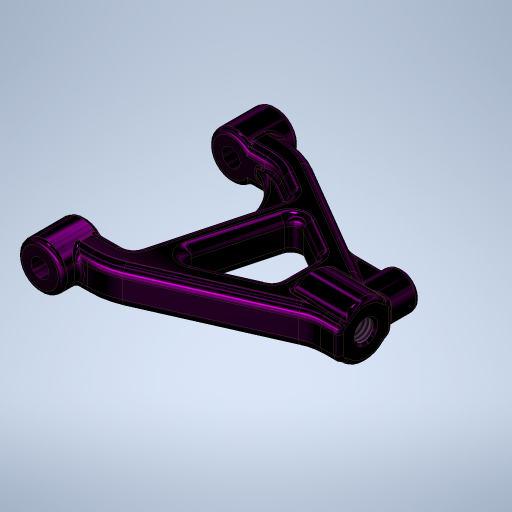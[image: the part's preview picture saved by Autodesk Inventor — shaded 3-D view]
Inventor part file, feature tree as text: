
AUTODESK INVENTOR PART (.ipt)
format: ipt  version: 2023.1 (Build 271208000, 208)  size: 1,221,120 bytes
history: native  units: in
note: dims shown in document units (in); Inventor stores cm internally (conversion verified against a paired STEP export)
features: fillet x19, sketch x11, extrude x6, rib x3, plane x2, hole x2, projected_geometry x2, chamfer x1
ambient origin geometry x8: Origin, YZ Plane, XZ Plane, XY Plane, X Axis, Y Axis, Z Axis, Center Point
bodies: Solid1 (feature_tree)
feature tree (46):
  extrude  "Extrusion1"  Depth=0.315in TaperAngle=0.0deg
  plane  "Work Plane1"
  extrude  "Extrusion2"  Depth=0.315in TaperAngle=0.0deg
  extrude  "Extrusion3"  Depth=0.375in
  fillet  "Fillet1"  Radius=0.5in
  fillet  "Fillet2"  Radius=1.5in
  fillet  "Fillet3"  Radius=0.1875in
  fillet  "Fillet4"  Radius=0.315in
  fillet  "Fillet5"  Radius=0.2in
  fillet  "Fillet6"  [1 undecoded]
  fillet  "Fillet7"  Radius=0.15in
  rib  "Rib1"
  fillet  "Fillet8"  Radius=0.25in
  fillet  "Fillet9"  Radius=0.315in
  rib  "Rib2"
  fillet  "Fillet10"  Radius=0.5in
  fillet  "Fillet11"  Radius=0.0625in
  extrude  "Extrusion4"  Depth=0.0625in
  fillet  "Fillet12"  Radius=0.0625in
  fillet  "Fillet13"  Radius=0.032in
  fillet  "Fillet14"  Radius=0.1in
  extrude  "Extrusion5"  Depth=0.032in
  plane  "Work Plane2"
  extrude  "Extrusion6"  Depth=0.1in
  fillet  "Fillet15"  Radius=0.032in
  rib  "Rib3"
  fillet  "Fillet16"  Radius=0.032in
  fillet  "Fillet17"  Radius=0.375in
  fillet  "Fillet18"  Radius=0.3875in
  hole  "Hole1"  [1 undecoded]
  fillet  "Fillet19"  Radius=0.032in
  hole  "Hole2"  [1 undecoded]
  chamfer  "Chamfer1"  Distance=0.135in
  sketch  "Sketch1"  dims[d0=0.315in d1=0.315in d2=0.0in]
  sketch  "Sketch2"  dims[d3=1.0in d4=0.315in d5=0.0in]
  sketch  "Sketch3"  dims[d6=0.742in d7=0.375in d8=0.5in d9=1.5in d10=0.1875in d11=0.315in d12=0.2in d13=105.0deg d14=0.15in d15=0.25in d16=0.0in d17=0.315in d18=0.5in d19=0.0625in]
  sketch  "Sketch4"  dims[d20=0.315in d21=0.0625in d22=0.0625in d23=0.032in d24=0.1in]
  sketch  "Sketch5"  dims[d25=0.1in d26=0.0in d27=0.0in d28=0.1in d29=0.1in d30=0.032in]
  sketch  "Sketch6"  dims[d31=0.032in d32=0.1in]
  sketch  "Sketch7"  dims[d33=0.1in d34=0.0in d35=0.0in d36=0.1in d37=0.1in d38=0.032in d39=0.032in d40=0.375in d41=0.3875in d42=0.0in]
  sketch  "Sketch8"  dims[d43=0.032in d44=0.032in d45=0.032in]
  sketch  "Sketch9"  dims[d46=0.125in d47=0.3875in d48=0.0in]
  sketch  "Sketch11"  dims[d49=0.2in]
  sketch  "Sketch12"  dims[d50=0.25in d51=0.135in d52=0.3875in d53=0.0in d54=0.015in d55=0.1in d56=0.1in d57=0.0in d58=0.0in d59=0.1in d60=0.1in d61=0.014in d62=0.032in d63=0.032in d64=0.0849in d65=0.224in d66=0.375in d67=0.25in d68=0.5635in d69=0.25in d70=0.8108in d71=0.014in d72=0.134in d73=0.328in d74=0.375in d75=0.25in d76=0.5635in d77=0.375in d78=0.8108in d79=0.015in d80=0.125in d81=45.0deg]
  projected_geometry  "Project Cut Edges1"
  projected_geometry  "Project Cut Edges2"
note: 3 required parameter values undecoded (feature->parameter linkage not recoverable at this tier; creation-order binding heuristic only, values carry confidence <= 0.55)
